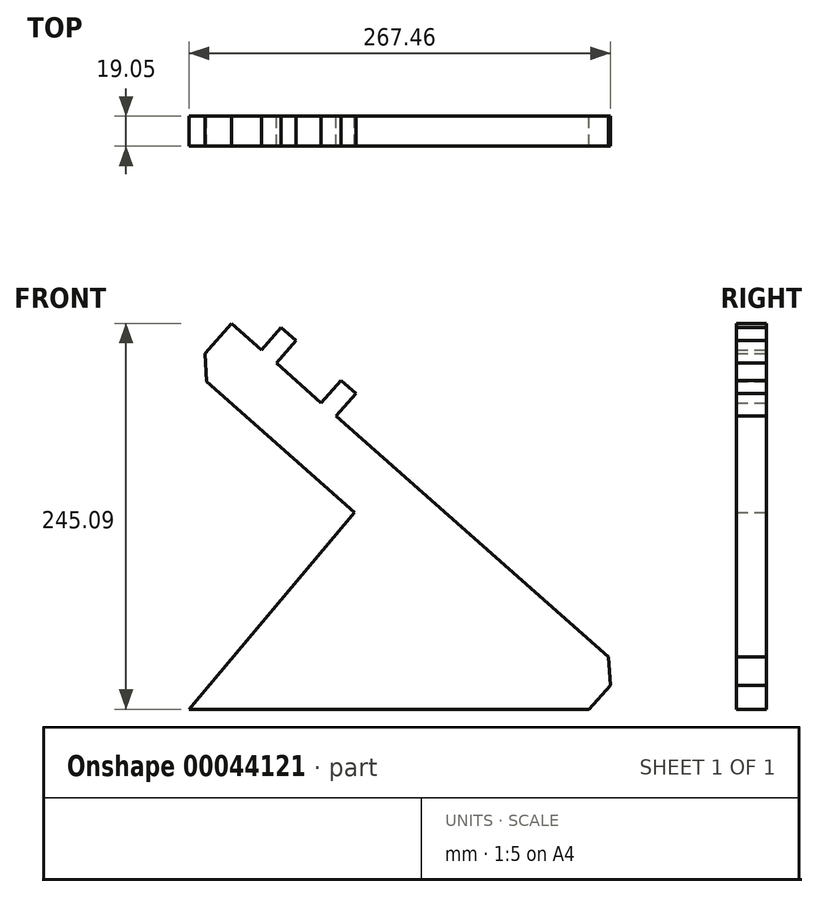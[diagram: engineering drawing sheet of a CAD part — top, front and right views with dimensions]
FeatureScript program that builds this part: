
annotation { "Feature Type Name" : "Feature", "Feature Type Description" : "" }
export const myFeature = defineFeature(function(context is Context, id is Id, definition is map)
    precondition{}
    {
        {
            var Q0;
            Q0=qCreatedBy(makeId("Front.planeOp"),FACE);
            var sketch = newSketch(context, id + "F0", { "sketchPlane" : qUnion([Q0])});
            skLineSegment(sketch, "E0", {"start": v(0, 125.07) * mm, "end": v(-104.95, 0) * mm});
            skLineSegment(sketch, "E1", {"start": v(-104.95, 0) * mm, "end": v(149.05, 0) * mm});
            skLineSegment(sketch, "E2", {"start": v(-59.14, 228.26) * mm, "end": v(-46.51, 242.53) * mm});
            skLineSegment(sketch, "E3", {"start": v(-46.51, 242.53) * mm, "end": v(-37, 234.11) * mm});
            skLineSegment(sketch, "E4", {"start": v(-37, 234.11) * mm, "end": v(-49.63, 219.85) * mm});
            skLineSegment(sketch, "E5", {"start": v(-49.63, 219.85) * mm, "end": v(-21.1, 194.6) * mm});
            skPoint(sketch, "E6", {"position": v(-21.1, 194.6) * mm});
            skLineSegment(sketch, "E7", {"start": v(-21.1, 194.6) * mm, "end": v(-8.47, 208.87) * mm});
            skLineSegment(sketch, "E8", {"start": v(-8.47, 208.87) * mm, "end": v(1.04, 200.45) * mm});
            skLineSegment(sketch, "E9", {"start": v(1.04, 200.45) * mm, "end": v(-11.58, 186.19) * mm});
            skLineSegment(sketch, "E10.trimOffspring", {"start": v(-11.58, 186.19) * mm, "end": v(161.41, 33.14) * mm});
            skLineSegment(sketch, "E11", {"start": v(149.05, 0) * mm, "end": v(162.5, 15.2) * mm});
            skLineSegment(sketch, "E12", {"start": v(-93.9, 208.14) * mm, "end": v(0, 125.07) * mm});
            skLineSegment(sketch, "E13", {"start": v(-21.1, 194.6) * mm, "end": v(-49.63, 219.85) * mm});
            skPoint(sketch, "E14", {"position": v(-59.14, 228.26) * mm});
            skLineSegment(sketch, "E15", {"start": v(-95, 226.07) * mm, "end": v(-78.16, 245.1) * mm});
            skLineSegment(sketch, "E16.trimOffspring", {"start": v(-59.14, 228.26) * mm, "end": v(-78.16, 245.1) * mm});
            skPoint(sketch, "E17", {"position": v(-95, 226.07) * mm});
            skPoint(sketch, "E18", {"position": v(-93.9, 208.14) * mm});
            skLineSegment(sketch, "E19", {"start": v(-95, 226.07) * mm, "end": v(-93.9, 208.14) * mm});
            skLineSegment(sketch, "E20", {"start": v(161.41, 33.14) * mm, "end": v(162.5, 15.2) * mm});
            skSolve(sketch);
        }
        {
            var Q0;
            Q0=makeQuery(id+"F0.imprint","IMPRINT",FACE,{"disambiguationData":[TD([[makeQuery(id+"F0.imprint","IMPRINT",EDGE,{"derivedFrom":sQuery(id+"F0.wireOp",EDGE,"E0")}),1.0]])]});
            extrude(context, id + "F1", {"entities" : qUnion([Q0]), "depth" : 19.05 * mm});
        }
    });
